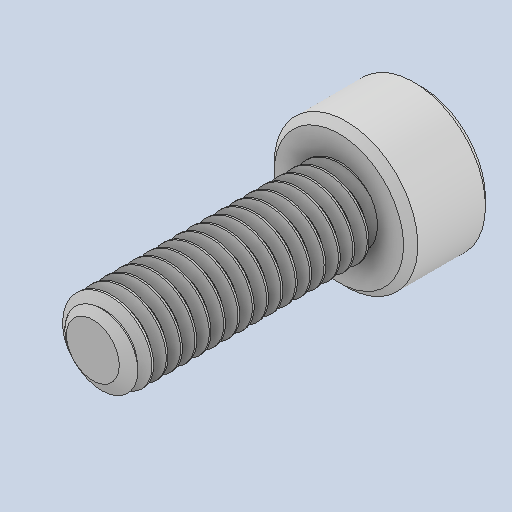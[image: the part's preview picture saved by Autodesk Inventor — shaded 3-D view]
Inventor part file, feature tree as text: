
AUTODESK INVENTOR PART (.ipt)
format: ipt  version: 2023 (Build 270158000, 158)  size: 623,104 bytes
history: native  units: in
note: dims shown in document units (in); Inventor stores cm internally (conversion verified against a paired STEP export)
features: chamfer x1
ambient origin geometry x8: Origin, YZ Plane, XZ Plane, XY Plane, X Axis, Y Axis, Z Axis, Center Point
bodies: Solid1 (feature_tree)
feature tree (1):
  chamfer  "Chamfer1"  [1 undecoded]
note: 1 required parameter value undecoded (feature->parameter linkage not recoverable at this tier; creation-order binding heuristic only, values carry confidence <= 0.55)
